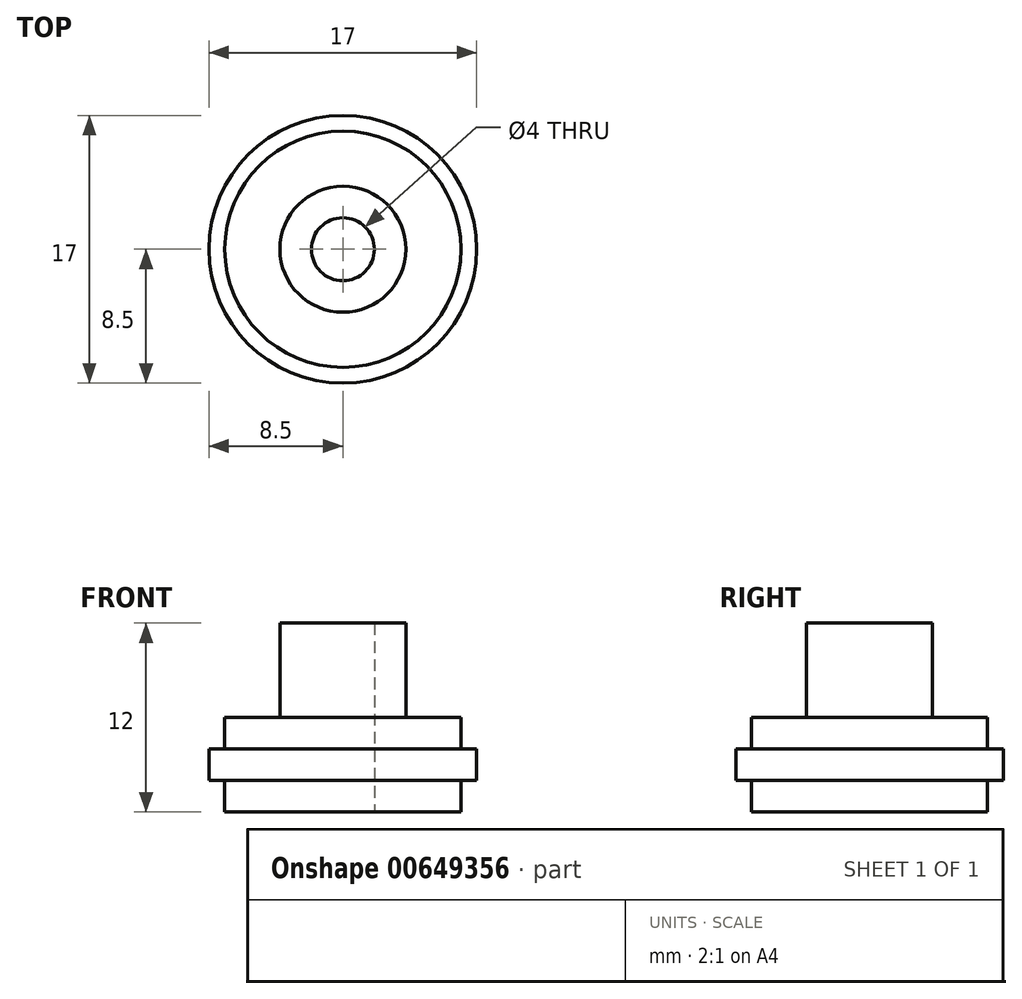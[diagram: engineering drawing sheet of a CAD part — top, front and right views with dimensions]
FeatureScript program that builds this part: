
annotation { "Feature Type Name" : "Feature", "Feature Type Description" : "" }
export const myFeature = defineFeature(function(context is Context, id is Id, definition is map)
    precondition{}
    {
        {
            var Q0;
            Q0=qCreatedBy(makeId("Top.planeOp"),FACE);
            var sketch = newSketch(context, id + "F0", { "sketchPlane" : qUnion([Q0])});
            skCircle(sketch, "E0", {"center": v(0, 0) * mm, "radius": 4 * mm});
            skCircle(sketch, "E1", {"center": v(0, 0) * mm, "radius": 2 * mm});
            skCircle(sketch, "E2", {"center": v(0, 0) * mm, "radius": 7.5 * mm});
            skCircle(sketch, "E3", {"center": v(0, 0) * mm, "radius": 8.5 * mm});
            skSolve(sketch);
        }
        {
            var Q0;
            Q0=makeQuery(id+"F0.imprint","IMPRINT",FACE,{"disambiguationData":[TD([[makeQuery(id+"F0.imprint","IMPRINT",EDGE,{"derivedFrom":sQuery(id+"F0.wireOp",EDGE,"E0")}),1.0]])]});
            extrude(context, id + "F1", {"entities" : qUnion([Q0]), "depth" : 12 * mm, "offsetDistance" : 25 * mm});
        }
        {
            var Q0;
            Q0=makeQuery(id+"F0.imprint","IMPRINT",FACE,{"disambiguationData":[TD([[makeQuery(id+"F0.imprint","IMPRINT",EDGE,{"derivedFrom":sQuery(id+"F0.wireOp",EDGE,"E0")}),-1.0]])]});
            extrude(context, id + "F2", {"entities" : qUnion([Q0]), "operationType" : NewBodyOperationType.ADD, "depth" : 6 * mm, "offsetDistance" : 25 * mm});
        }
        {
            var Q0;
            Q0=makeQuery(id+"F0.imprint","IMPRINT",FACE,{"disambiguationData":[TD([[makeQuery(id+"F0.imprint","IMPRINT",EDGE,{"derivedFrom":sQuery(id+"F0.wireOp",EDGE,"E2")}),-1.0]])]});
            extrude(context, id + "F3", {"entities" : qUnion([Q0]), "operationType" : NewBodyOperationType.ADD, "depth" : 4 * mm, "offsetDistance" : 25 * mm, "hasSecondDirection" : true, "secondDirectionOppositeDirection" : false, "secondDirectionDepth" : 2 * mm});
        }
    });
